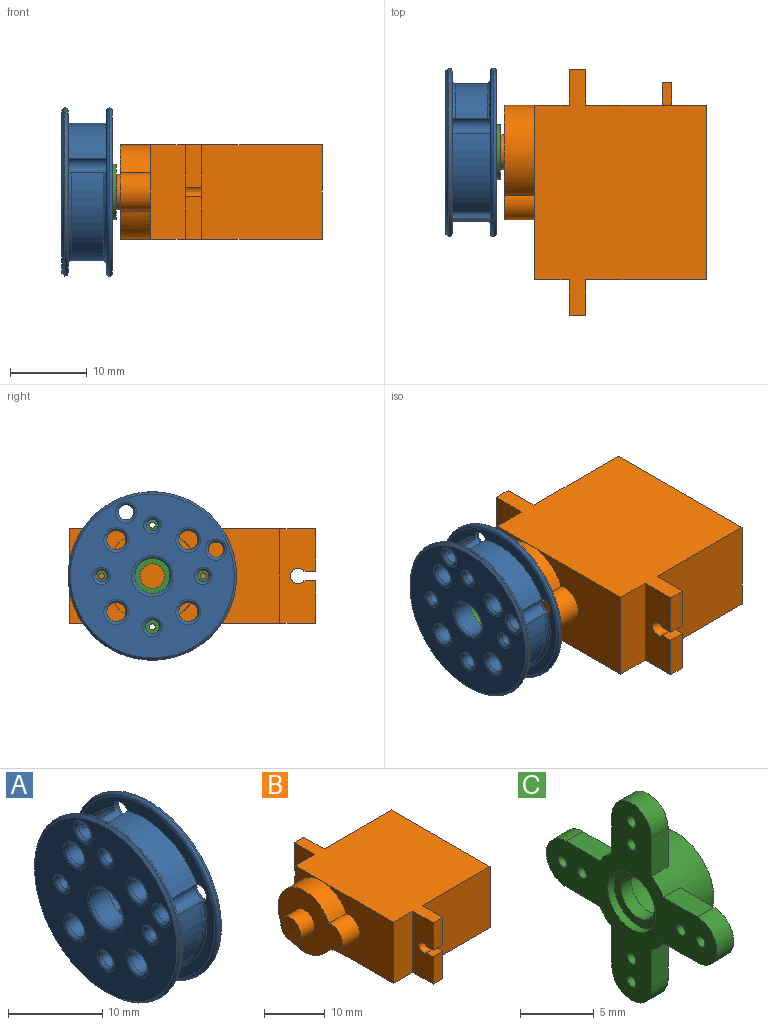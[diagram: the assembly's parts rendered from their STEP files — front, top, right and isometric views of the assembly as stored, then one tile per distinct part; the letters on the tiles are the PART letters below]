
ASSEMBLY  parts=3 mates=1
PART A: 67 faces, bbox 6.6x23.8x23.8 mm
  f0: cylinder r=9mm len=10.38mm, axis (1,0,0), area 60.7mm2, adj f5,f6,f33,f34
  f1: plane 21.2x21.2mm, normal (1,0,0), area 165.4mm2, adj f8,f12,f16,f17,f18,f19,f22,f36
  f2: cylinder r=9mm len=18mm, axis (1,0,0), area 169.7mm2, adj f33,f34,f62,f66
  f3: cylinder r=11mm len=22mm, axis (1,0,0), area 6.9mm2, adj f35,f65
  f4: plane 21.4x21.4mm, normal (-1,0,0), area 272.4mm2, adj f35,f44,f45,f50,f51,f52,f53,f54
  f5: plane 21.2x21.2mm, normal (1,0,0), area 78.8mm2, adj f0,f33,f34,f65,f66
  f6: plane 21.2x21.2mm, normal (-1,0,0), area 78.8mm2, adj f0,f33,f34,f62,f64
  f7: plane 3.4x3.08mm, normal (0,-1,0), area 10.5mm2, adj f8,f20,f21,f37
  f8: cylinder r=3.9mm len=3.8mm, axis (-1,0,0), area 5.3mm2, adj f1,f7,f9,f20,f37,f42
  f9: plane 3.4x3.08mm, normal (0,0,-1), area 10.5mm2, adj f8,f10,f20,f42
  f10: cylinder r=2.2mm len=4.4mm, axis (-1,0,0), area 23.5mm2, adj f9,f11,f20,f41
  f11: plane 3.4x3.08mm, normal (0,0,1), area 10.5mm2, adj f10,f12,f20,f40
  f12: cylinder r=3.9mm len=3.8mm, axis (-1,0,0), area 5.3mm2, adj f1,f11,f13,f20,f40,f61
  f13: plane 3.4x3.08mm, normal (0,-1,0), area 10.5mm2, adj f12,f14,f20,f61
  f14: cylinder r=2.2mm len=4.4mm, axis (-1,0,0), area 23.5mm2, adj f13,f15,f20,f60
  f15: plane 3.4x3.08mm, normal (0,1,0), area 10.5mm2, adj f14,f16,f20,f59
  f16: cylinder r=3.9mm len=3.8mm, axis (-1,0,0), area 5.4mm2, adj f1,f15,f17,f20,f59
  f17: plane 3.8x3.08mm, normal (0,0,1), area 11.7mm2, adj f1,f16,f18,f20
  f18: cylinder r=2.2mm len=4.4mm, axis (-1,0,0), area 26.3mm2, adj f1,f17,f19,f20
  f19: plane 3.8x3.08mm, normal (0,0,-1), area 11.7mm2, adj f1,f18,f20,f22
  f20: plane 17x17mm, normal (1,0,0), area 99.7mm2, adj f7,f8,f9,f10,f11,f12,f13,f14
  f21: cylinder r=2.2mm len=4.4mm, axis (-1,0,0), area 23.5mm2, adj f7,f20,f23,f38
  f22: cylinder r=3.9mm len=3.8mm, axis (-1,0,0), area 5.4mm2, adj f1,f19,f20,f23,f39
  f23: plane 3.4x3.08mm, normal (0,1,0), area 10.5mm2, adj f20,f21,f22,f39
  f24: cylinder r=0.75mm len=2.4mm, axis (1,0,0), area 11.3mm2, adj f20,f56
  f25: cylinder r=0.75mm len=2.4mm, axis (1,0,0), area 11.3mm2, adj f20,f58
  f26: cylinder r=0.91mm len=2.4mm, axis (1,0,0), area 13.7mm2, adj f20,f57
  f27: cylinder r=0.75mm len=2.4mm, axis (1,0,0), area 11.3mm2, adj f20,f55
  f28: cylinder r=2.3mm len=4.6mm, axis (1,0,0), area 34.7mm2, adj f20,f54
  f29: cylinder r=1.25mm len=5.8mm, axis (-1,0,0), area 45.6mm2, adj f49,f53
  f30: cylinder r=1.25mm len=5.8mm, axis (-1,0,0), area 45.6mm2, adj f48,f52
  f31: cylinder r=1.25mm len=5.8mm, axis (-1,0,0), area 45.6mm2, adj f47,f51
  f32: cylinder r=1.25mm len=5.8mm, axis (-1,0,0), area 45.6mm2, adj f46,f50
  f33: cylinder r=1mm len=5.8mm, axis (-1,0,0), area 20.3mm2, adj f0,f2,f5,f6,f43,f44,f62,f66
  f34: cylinder r=1mm len=5.8mm, axis (-1,0,0), area 20.3mm2, adj f0,f2,f5,f6,f36,f45,f62,f66
  f35: cone r=10.7mm half-angle=45deg, axis (1,0,0), area 28.9mm2, adj f3,f4
  f36: torus R=1.4mm, axis (1,0,0), area 4.5mm2, adj f1,f34,f38
  f37: cylinder r=0.4mm len=3.39mm, axis (0,0,1), area 2mm2, adj f1,f7,f8,f38
  f38: torus R=2.6mm, axis (1,0,0), area 4.6mm2, adj f1,f21,f36,f37,f39
  f39: cylinder r=0.4mm len=3.39mm, axis (0,0,-1), area 2mm2, adj f1,f22,f23,f38
  f40: cylinder r=0.4mm len=3.39mm, axis (0,1,0), area 2mm2, adj f1,f11,f12,f41
  f41: torus R=2.6mm, axis (1,0,0), area 4.6mm2, adj f1,f10,f40,f42
  f42: cylinder r=0.4mm len=3.39mm, axis (0,-1,0), area 2mm2, adj f1,f8,f9,f41
  f43: torus R=1.4mm, axis (1,0,0), area 4.5mm2, adj f1,f33
  f44: torus R=1.4mm, axis (-1,0,0), area 4.5mm2, adj f4,f33
  f45: torus R=1.4mm, axis (-1,0,0), area 4.5mm2, adj f4,f34
  f46: torus R=1.65mm, axis (1,0,0), area 5.5mm2, adj f1,f32
  f47: torus R=1.65mm, axis (1,0,0), area 5.5mm2, adj f1,f31
  f48: torus R=1.65mm, axis (1,0,0), area 5.5mm2, adj f1,f30
  f49: torus R=1.65mm, axis (1,0,0), area 5.5mm2, adj f1,f29
  f50: torus R=1.65mm, axis (-1,0,0), area 5.5mm2, adj f4,f32
  f51: torus R=1.65mm, axis (-1,0,0), area 5.5mm2, adj f4,f31
  f52: torus R=1.65mm, axis (-1,0,0), area 5.5mm2, adj f4,f30
  f53: torus R=1.65mm, axis (-1,0,0), area 5.5mm2, adj f4,f29
  f54: torus R=2.7mm, axis (-1,0,0), area 9.7mm2, adj f4,f28
  f55: torus R=1.15mm, axis (-1,0,0), area 3.5mm2, adj f4,f27
  f56: torus R=1.15mm, axis (-1,0,0), area 3.5mm2, adj f4,f24
  f57: torus R=1.31mm, axis (-1,0,0), area 4.2mm2, adj f4,f26
  f58: torus R=1.15mm, axis (-1,0,0), area 3.5mm2, adj f4,f25
  f59: cylinder r=0.4mm len=3.39mm, axis (0,0,-1), area 2mm2, adj f1,f15,f16,f60
  f60: torus R=2.6mm, axis (1,0,0), area 4.6mm2, adj f1,f14,f59,f61
  f61: cylinder r=0.4mm len=3.39mm, axis (0,0,1), area 2mm2, adj f1,f12,f13,f60
  f62: torus R=9.4mm, axis (1,0,0), area 25.9mm2, adj f2,f6,f33,f34
  f63: torus R=10.6mm, axis (1,0,0), area 42.9mm2, adj f1,f64
  f64: torus R=10.6mm, axis (1,0,0), area 42.9mm2, adj f6,f63
  f65: torus R=10.6mm, axis (-1,0,0), area 42.9mm2, adj f3,f5
  f66: torus R=9.4mm, axis (-1,0,0), area 25.9mm2, adj f2,f5,f33,f34
PART B: 34 faces, bbox 29.6x32.2x12.3 mm
  f0: plane 16.65x12.3mm, normal (-1,0,0), area 134mm2, adj f5,f16,f17,f24,f25
  f1: plane 6.15x6.15mm, normal (-1,0,0), area 8.1mm2, adj f15,f16,f24
  f2: plane 5.5x2.2mm, normal (0,-1,0), area 12.1mm2, adj f6,f8,f16,f23
  f3: plane 5.5x2.2mm, normal (0,1,0), area 12.1mm2, adj f12,f14,f16,f19
  f4: plane 6.15x6.15mm, normal (-1,0,0), area 8.1mm2, adj f15,f17,f24
  f5: plane 12.3x4.5mm, normal (0,-1,0), area 55.3mm2, adj f0,f6,f16,f17
  f6: plane 12.3x4.7mm, normal (-1,0,0), area 52.9mm2, adj f2,f5,f7,f16,f17,f21,f22,f23
  f7: plane 5.5x2.2mm, normal (0,-1,0), area 12.1mm2, adj f6,f8,f17,f22
  f8: plane 12.3x4.7mm, normal (1,0,0), area 52.9mm2, adj f2,f7,f9,f16,f17,f21,f22,f23
  f9: plane 15.7x12.3mm, normal (0,-1,0), area 193.1mm2, adj f8,f10,f16,f17
  f10: plane 22.8x12.3mm, normal (1,0,0), area 280.4mm2, adj f9,f11,f16,f17
  f11: plane 15.7x12.3mm, normal (0,1,0), area 188.8mm2, adj f10,f12,f16,f17,f29,f30,f31,f32
  f12: plane 12.3x4.7mm, normal (1,0,0), area 52.9mm2, adj f3,f11,f13,f16,f17,f18,f19,f20
  f13: plane 5.5x2.2mm, normal (0,1,0), area 12.1mm2, adj f12,f14,f17,f20
  f14: plane 12.3x4.7mm, normal (-1,0,0), area 52.9mm2, adj f3,f13,f15,f16,f17,f18,f19,f20
  f15: plane 12.3x4.5mm, normal (0,1,0), area 55.3mm2, adj f1,f4,f14,f16,f17
  f16: plane 32.2x22.4mm, normal (0,0,1), area 531.4mm2, adj f0,f1,f2,f3,f5,f6,f8,f9
  f17: plane 32.2x22.4mm, normal (0,0,-1), area 531.4mm2, adj f0,f4,f5,f6,f7,f8,f9,f10
  f18: cylinder r=1mm len=2.2mm, axis (-1,0,0), area 10.7mm2, adj f12,f14,f19,f20
  f19: plane 2.2x1.54mm, normal (0,0,-1), area 3.4mm2, adj f3,f12,f14,f18
  f20: plane 2.2x1.54mm, normal (0,0,1), area 3.4mm2, adj f12,f13,f14,f18
  f21: cylinder r=1mm len=2.2mm, axis (-1,0,0), area 10.7mm2, adj f6,f8,f22,f23
  f22: plane 2.2x1.54mm, normal (0,0,1), area 3.4mm2, adj f6,f7,f8,f21
  f23: plane 2.2x1.54mm, normal (0,0,-1), area 3.4mm2, adj f2,f6,f8,f21
  f24: cylinder r=6.15mm len=12.3mm, axis (1,0,0), area 134.7mm2, adj f0,f1,f4,f25,f26
  f25: cylinder r=2.5mm len=5mm, axis (1,0,0), area 36.6mm2, adj f0,f24,f26
  f26: plane 14.95x12.3mm, normal (-1,0,0), area 113.6mm2, adj f24,f25,f27
  f27: cylinder r=2.3mm len=4.6mm, axis (1,0,0), area 46.2mm2, adj f26,f28
  f28: plane 4.6x4.6mm, normal (-1,0,0), area 16.6mm2, adj f27
  f29: plane 3.6x3mm, normal (-1,0,0), area 10.8mm2, adj f11,f30,f32,f33
  f30: plane 3x1.2mm, normal (0,0,1), area 3.6mm2, adj f11,f29,f31,f33
  f31: plane 3.6x3mm, normal (1,0,0), area 10.8mm2, adj f11,f30,f32,f33
  f32: plane 3x1.2mm, normal (0,0,-1), area 3.6mm2, adj f11,f29,f31,f33
  f33: plane 3.6x1.2mm, normal (0,1,0), area 4.3mm2, adj f29,f30,f31,f32
PART C: 32 faces, bbox 4.3x16.4x16.4 mm
  f0: plane 4.6x4.6mm, normal (1,0,0), area 8.6mm2, adj f24,f26
  f1: plane 5.14x3.8mm, normal (1,0,0), area 15.6mm2, adj f7,f8,f9,f16,f17,f30
  f2: plane 5.14x3.8mm, normal (1,0,0), area 15.6mm2, adj f9,f10,f11,f13,f21,f31
  f3: plane 5.14x3.8mm, normal (1,0,0), area 15.6mm2, adj f4,f9,f12,f19,f20,f28
  f4: plane 3.24x1.6mm, normal (0,0,1), area 5.2mm2, adj f3,f9,f22,f28
  f5: plane 3.24x1.6mm, normal (0,-1,0), area 5.2mm2, adj f9,f22,f23,f29
  f6: plane 3.24x1.6mm, normal (0,1,0), area 5.2mm2, adj f9,f22,f23,f29
  f7: plane 3.24x1.6mm, normal (0,0,1), area 5.2mm2, adj f1,f9,f22,f30
  f8: plane 3.24x1.6mm, normal (0,0,-1), area 5.2mm2, adj f1,f9,f22,f30
  f9: cylinder r=3.6mm len=7.2mm, axis (1,0,0), area 71.6mm2, adj f1,f2,f3,f4,f5,f6,f7,f8
  f10: plane 3.24x1.6mm, normal (0,1,0), area 5.2mm2, adj f2,f9,f22,f31
  f11: plane 3.24x1.6mm, normal (0,-1,0), area 5.2mm2, adj f2,f9,f22,f31
  f12: plane 3.24x1.6mm, normal (0,0,-1), area 5.2mm2, adj f3,f9,f22,f28
  f13: cylinder r=0.4mm len=1.6mm, axis (1,0,0), area 4mm2, adj f2,f22
  f14: cylinder r=0.4mm len=1.6mm, axis (1,0,0), area 4mm2, adj f22,f23
  f15: cylinder r=0.4mm len=1.6mm, axis (1,0,0), area 4mm2, adj f22,f23
  f16: cylinder r=0.4mm len=1.6mm, axis (1,0,0), area 4mm2, adj f1,f22
  f17: cylinder r=0.4mm len=1.6mm, axis (1,0,0), area 4mm2, adj f1,f22
  f18: cylinder r=2.3mm len=4.6mm, axis (1,0,0), area 8.7mm2, adj f22,f25
  f19: cylinder r=0.4mm len=1.6mm, axis (1,0,0), area 4mm2, adj f3,f22
  f20: cylinder r=0.4mm len=1.6mm, axis (1,0,0), area 4mm2, adj f3,f22
  f21: cylinder r=0.4mm len=1.6mm, axis (1,0,0), area 4mm2, adj f2,f22
  f22: plane 16.4x16.4mm, normal (-1,0,0), area 86.5mm2, adj f4,f5,f6,f7,f8,f9,f10,f11
  f23: plane 5.14x3.8mm, normal (1,0,0), area 15.6mm2, adj f5,f6,f9,f14,f15,f29
  f24: cylinder r=1.6mm len=3.2mm, axis (1,0,0), area 10.1mm2, adj f0,f25
  f25: plane 4.6x4.6mm, normal (-1,0,0), area 8.6mm2, adj f18,f24
  f26: cylinder r=2.3mm len=4.6mm, axis (-1,0,0), area 39mm2, adj f0,f27
  f27: plane 7.2x7.2mm, normal (1,0,0), area 24.1mm2, adj f9,f26
  f28: cylinder r=1.9mm len=3.8mm, axis (-1,0,0), area 9.6mm2, adj f3,f4,f12,f22
  f29: cylinder r=1.9mm len=3.8mm, axis (-1,0,0), area 9.6mm2, adj f5,f6,f22,f23
  f30: cylinder r=1.9mm len=3.8mm, axis (-1,0,0), area 9.6mm2, adj f1,f7,f8,f22
  f31: cylinder r=1.9mm len=3.8mm, axis (-1,0,0), area 9.6mm2, adj f2,f10,f11,f22
PLACE A t=(-5.17,0.95,0.7)mm
PLACE B t=(-5.17,0.95,0.7)mm
PLACE C t=(-5.17,0.95,0.7)mm
MATE fastened A.f28 <-> C.f18  axis (1,0,0) through (-13.97,6.2,0.7)mm
